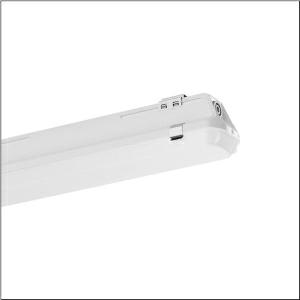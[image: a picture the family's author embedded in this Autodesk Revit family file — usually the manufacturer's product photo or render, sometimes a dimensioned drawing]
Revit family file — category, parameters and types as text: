
# Revit family: monsun_r__21_51fb20dl440j_72cd
name_source: partatom
category: Lighting Fixtures
units: mm (PartAtom-declared; Revit-internal decimal feet)

## family parameters
Cut with Voids When Loaded = No
Host = Face
Light Source = No
Part Type = Normal
Room Calculation Point = No
Round Connector Dimension = Use Diameter
Shared = No

## types (1)
- --- (1 x LED, 4320 lm, 29.7 W, 4000K)
    Apparent Load = 30 VA
    CIE Flux Codes = 45 75 93 94 100
    Color Rendering = 80
    Color Temperature = 4000K
    Default Elevation = 1800 mm
    Description = Monsun® 21, damp-proof luminaire, chain hanger, primary optical cover: enclosure, of PC, light emission: direct distribution, primary light characteristic: symmetric, installation type: suspended mounting, surface-mounted, horizontal mounting, vertical mounting, LED, rated luminous flux: 4.320lm, luminous efficacy: 144lm/W, light colour: 840, colour temperature: 4000K, control gear: ECG DALI, with terminal, 5-pole, max. 2.5mm², mains connection: 220..240V, AC, 50/60Hz, rated input power: 30W, housing, of glass-fibre reinforced plastic, uncoated, bright grey, incl. chain hanger, length: 1.299mm, width: 90mm, height: 88mm, clip for enclosure, of stainless steel (V2A), ceiling mounting element, of stainless steel (V2A), chain hanger, of stainless steel (V2A), protection rating (complete): IP66, insulation class (complete): insulation class I (protective earthing), certification: CE, ENEC, VDE, UKCA, protection symbol: D, impact resistance: IK08, permissible operating ambient temperature: -25..+35°C, standard: EN 50419, EN 60598-2-1, corresponds to IFS (International Featured Standards) requirements for safety and quality in the food industry, for indoor or canopied outdoor use, no direct snow, no direct sun, no direct rain, contact your sales advisor before using the luminaires in applications with unclear chemical exposure, large temperature fluctuations or condensation-forming humidity, LABS conformity tested according to VDMA 24364:2018-05, packaging unit: 1 piece
    Height = 88 mm
    Lamp = 1 x LED
    Lamp Light Flux = 4320 lm
    Lamp Power = 29.7 W
    Lamp count = 1
    Length = 1299 mm
    Luminous efficacy = 145 lm/W
    Manufacturer = Siteco
    ModVariant = No
    Model = 51FB20DL440J
    Mounting Place = Ceiling
    Mounting Type = Surface mounted
    Number of Poles = 1
    OnlyDefault = Yes
    Power Factor = 1
    Product Name = Monsun® 21
    Product group = damp-proof luminaire
    ProductGroupID = 300
    Protection Class = Protection class I
    Protection Degree = IP 66
    RLX_Detail_Level = 1
    RLX_Emergency_Light_Flux = 0 lm
    RLX_Emergency_Type = 0
    RLX_Emergency_Type_DB = No
    RlxData = <blob elided: 93321 chars, md5=192ec275>
    Socket = socket
    Standby Power = 0 W
    System Light Flux = 4320 lm
    System Power = 30 W
    Type Comments = factory setting: luminous flux: 100 % | dim-lin: 254 | 199 mA
    Type Image = l_1006717.jpg
    URL = http://relux.com
    VarID = @adj_077945
    Voltage = 0 V
    Weight = 0.00 kg
    Width = 90 mm

## geometry (parser evidence)
native form markers: Blend x4, Sweep x13
no freeform markers — native parametric forms only
